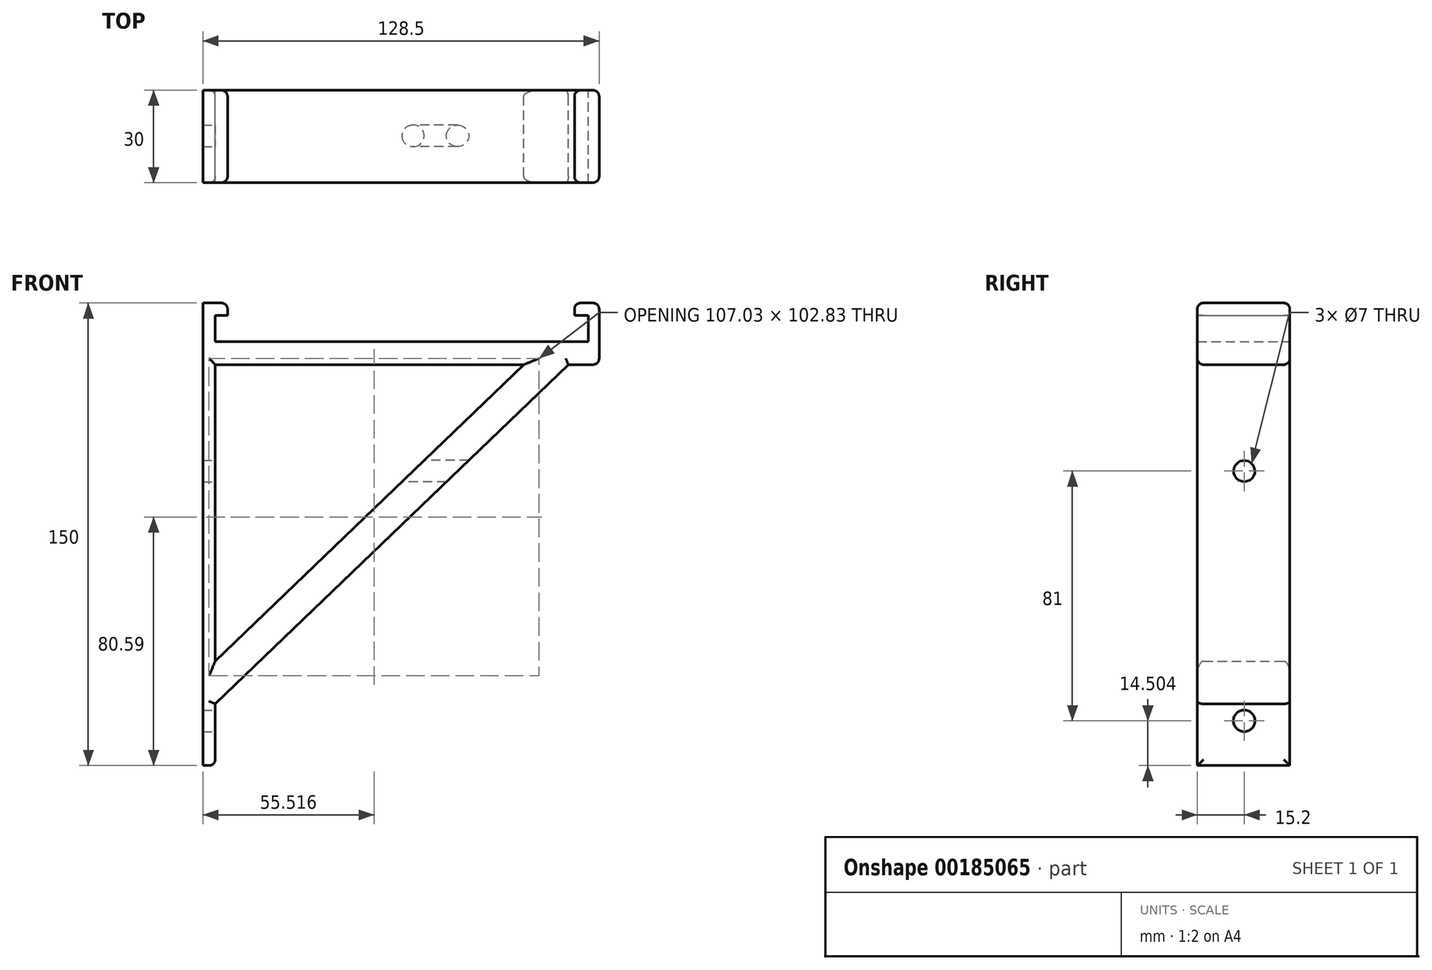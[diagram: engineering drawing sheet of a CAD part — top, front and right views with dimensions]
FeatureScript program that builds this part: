
annotation { "Feature Type Name" : "Feature", "Feature Type Description" : "" }
export const myFeature = defineFeature(function(context is Context, id is Id, definition is map)
    precondition{}
    {
        {
            var Q0;
            Q0=qCreatedBy(makeId("Front.planeOp"),FACE);
            var sketch = newSketch(context, id + "F0", { "sketchPlane" : qUnion([Q0])});
            skLineSegment(sketch, "E0", {"start": v(-57.97, 32.57) * mm, "end": v(-57.97, 24.07) * mm});
            skLineSegment(sketch, "E1", {"start": v(-57.97, 24.07) * mm, "end": v(63.03, 24.07) * mm});
            skLineSegment(sketch, "E2", {"start": v(63.03, 24.07) * mm, "end": v(63.03, 32.57) * mm});
            skLineSegment(sketch, "E3", {"start": v(63.03, 32.57) * mm, "end": v(58.53, 32.57) * mm});
            skLineSegment(sketch, "E4", {"start": v(58.53, 32.57) * mm, "end": v(58.53, 36.57) * mm});
            skLineSegment(sketch, "E5", {"start": v(58.53, 36.57) * mm, "end": v(66.53, 36.57) * mm});
            skLineSegment(sketch, "E6", {"start": v(66.53, 36.57) * mm, "end": v(66.53, 16.57) * mm});
            skLineSegment(sketch, "E7", {"start": v(-61.97, 36.57) * mm, "end": v(-53.97, 36.57) * mm});
            skLineSegment(sketch, "E8", {"start": v(-53.97, 36.57) * mm, "end": v(-53.97, 32.57) * mm});
            skLineSegment(sketch, "E9", {"start": v(-61.97, 36.57) * mm, "end": v(-61.97, 36.57) * mm});
            skLineSegment(sketch, "E10", {"start": v(-61.97, 36.57) * mm, "end": v(-61.97, -113.43) * mm});
            skLineSegment(sketch, "E11", {"start": v(-61.97, -113.43) * mm, "end": v(-61.97, -113.43) * mm});
            skLineSegment(sketch, "E12", {"start": v(66.53, 16.57) * mm, "end": v(56.53, 16.57) * mm});
            skLineSegment(sketch, "E13", {"start": v(56.53, 16.57) * mm, "end": v(-57.97, -93.43) * mm});
            skLineSegment(sketch, "E14", {"start": v(-57.97, -93.43) * mm, "end": v(-57.97, -113.43) * mm});
            skLineSegment(sketch, "E15", {"start": v(-57.97, -113.43) * mm, "end": v(-61.97, -113.43) * mm});
            skLineSegment(sketch, "E16", {"start": v(-57.97, 16.57) * mm, "end": v(-57.97, -79.56) * mm});
            skLineSegment(sketch, "E17", {"start": v(-57.97, -79.56) * mm, "end": v(42.1, 16.57) * mm});
            skLineSegment(sketch, "E18", {"start": v(42.1, 16.57) * mm, "end": v(-57.97, 16.57) * mm});
            skLineSegment(sketch, "E19", {"start": v(-53.97, 32.57) * mm, "end": v(-57.97, 32.57) * mm});
            skSolve(sketch);
        }
        {
            var Q0;
            Q0=makeQuery(id+"F0.imprint","IMPRINT",FACE,{"disambiguationData":[TD([[makeQuery(id+"F0.imprint","IMPRINT",EDGE,{"derivedFrom":sQuery(id+"F0.wireOp",EDGE,"E0")}),-1.0]])]});
            extrude(context, id + "F1", {"entities" : qUnion([Q0]), "depth" : 30 * mm});
        }
        {
            var Q0;
            Q0=qCreatedBy(makeId("Right.planeOp"),FACE);
            var sketch = newSketch(context, id + "F2", { "sketchPlane" : qUnion([Q0])});
            skCircle(sketch, "E20", {"center": v(-14.8, -98.93) * mm, "radius": 3.5 * mm});
            skCircle(sketch, "E21", {"center": v(-14.8, -17.93) * mm, "radius": 3.5 * mm});
            skSolve(sketch);
        }
        {
            var Q0;
            Q0 = qSketchRegion(id + "F2", true);
            extrude(context, id + "F3", {"entities" : qUnion([Q0]), "operationType" : NewBodyOperationType.REMOVE, "oppositeDirection" : true, "depth" : 73.1 * mm});
        }
        {
            var Q0;
            Q0 = qSketchRegion(id + "F2", true);
            extrude(context, id + "F4", {"entities" : qUnion([Q0]), "operationType" : NewBodyOperationType.REMOVE, "depth" : 25 * mm, "hasSecondDirection" : true, "secondDirectionOppositeDirection" : true, "secondDirectionDepth" : 25 * mm});
        }
        {
            var Q0;
            Q0=makeQuery(id+"F1.opExtrude","SWEPT_EDGE",EDGE,{"disambiguationData":[OSD([sQuery(id+"F0.wireOp",EDGE,"E5"),sQuery(id+"F0.wireOp",EDGE,"E6")])]});
            var Q1;
            Q1=makeQuery(id+"F1.opExtrude","SWEPT_EDGE",EDGE,{"disambiguationData":[OSD([sQuery(id+"F0.wireOp",EDGE,"E4"),sQuery(id+"F0.wireOp",EDGE,"E5")])]});
            var Q2;
            Q2=makeQuery(id+"F1.opExtrude","CAP_EDGE",EDGE,{"disambiguationData":[OSD([sQuery(id+"F0.wireOp",EDGE,"E6")])],"isStart":false});
            var Q3;
            Q3=makeQuery(id+"F1.opExtrude","CAP_EDGE",EDGE,{"disambiguationData":[OSD([sQuery(id+"F0.wireOp",EDGE,"E5")])],"isStart":false});
            var Q4;
            Q4=makeQuery(id+"F1.opExtrude","CAP_EDGE",EDGE,{"disambiguationData":[OSD([sQuery(id+"F0.wireOp",EDGE,"E5")])],"isStart":true});
            var Q5;
            Q5=makeQuery(id+"F1.opExtrude","CAP_EDGE",EDGE,{"disambiguationData":[OSD([sQuery(id+"F0.wireOp",EDGE,"E6")])],"isStart":true});
            var Q6;
            Q6=makeQuery(id+"F1.opExtrude","CAP_EDGE",EDGE,{"disambiguationData":[OSD([sQuery(id+"F0.wireOp",EDGE,"E4")])],"isStart":true});
            var Q7;
            Q7=makeQuery(id+"F1.opExtrude","CAP_EDGE",EDGE,{"disambiguationData":[OSD([sQuery(id+"F0.wireOp",EDGE,"E4")])],"isStart":false});
            var Q8;
            Q8=makeQuery(id+"F1.opExtrude","SWEPT_EDGE",EDGE,{"disambiguationData":[OSD([sQuery(id+"F0.wireOp",EDGE,"E6"),sQuery(id+"F0.wireOp",EDGE,"E12")])]});
            var Q9;
            Q9=makeQuery(id+"F1.opExtrude","CAP_EDGE",EDGE,{"disambiguationData":[OSD([sQuery(id+"F0.wireOp",EDGE,"E12")])],"isStart":false});
            var Q10;
            Q10=makeQuery(id+"F1.opExtrude","CAP_EDGE",EDGE,{"disambiguationData":[OSD([sQuery(id+"F0.wireOp",EDGE,"E12")])],"isStart":true});
            var Q11;
            Q11=makeQuery(id+"F1.opExtrude","CAP_EDGE",EDGE,{"disambiguationData":[OSD([sQuery(id+"F0.wireOp",EDGE,"E18")])],"isStart":false});
            var Q12;
            Q12=makeQuery(id+"F1.opExtrude","CAP_EDGE",EDGE,{"disambiguationData":[OSD([sQuery(id+"F0.wireOp",EDGE,"E18")])],"isStart":true});
            var Q13;
            Q13=makeQuery(id+"F1.opExtrude","CAP_EDGE",EDGE,{"disambiguationData":[OSD([sQuery(id+"F0.wireOp",EDGE,"E13")])],"isStart":false});
            var Q14;
            Q14=makeQuery(id+"F1.opExtrude","CAP_EDGE",EDGE,{"disambiguationData":[OSD([sQuery(id+"F0.wireOp",EDGE,"E17")])],"isStart":false});
            var Q15;
            Q15=makeQuery(id+"F1.opExtrude","CAP_EDGE",EDGE,{"disambiguationData":[OSD([sQuery(id+"F0.wireOp",EDGE,"E16")])],"isStart":false});
            var Q16;
            Q16=makeQuery(id+"F1.opExtrude","CAP_EDGE",EDGE,{"disambiguationData":[OSD([sQuery(id+"F0.wireOp",EDGE,"E16")])],"isStart":true});
            var Q17;
            Q17=makeQuery(id+"F1.opExtrude","CAP_EDGE",EDGE,{"disambiguationData":[OSD([sQuery(id+"F0.wireOp",EDGE,"E13")])],"isStart":true});
            var Q18;
            Q18=makeQuery(id+"F1.opExtrude","CAP_EDGE",EDGE,{"disambiguationData":[OSD([sQuery(id+"F0.wireOp",EDGE,"E17")])],"isStart":true});
            var Q19;
            Q19=makeQuery(id+"F1.opExtrude","SWEPT_EDGE",EDGE,{"disambiguationData":[OSD([sQuery(id+"F0.wireOp",EDGE,"E14"),sQuery(id+"F0.wireOp",EDGE,"E15")])]});
            var Q20;
            Q20=makeQuery(id+"F1.opExtrude","CAP_EDGE",EDGE,{"disambiguationData":[OSD([sQuery(id+"F0.wireOp",EDGE,"E14")])],"isStart":true});
            var Q21;
            Q21=makeQuery(id+"F1.opExtrude","CAP_EDGE",EDGE,{"disambiguationData":[OSD([sQuery(id+"F0.wireOp",EDGE,"E14")])],"isStart":false});
            var Q22;
            Q22=makeQuery(id+"F1.opExtrude","CAP_EDGE",EDGE,{"disambiguationData":[OSD([sQuery(id+"F0.wireOp",EDGE,"E7")])],"isStart":true});
            var Q23;
            Q23=makeQuery(id+"F1.opExtrude","CAP_EDGE",EDGE,{"disambiguationData":[OSD([sQuery(id+"F0.wireOp",EDGE,"E8")])],"isStart":true});
            var Q24;
            Q24=makeQuery(id+"F1.opExtrude","SWEPT_EDGE",EDGE,{"disambiguationData":[OSD([sQuery(id+"F0.wireOp",EDGE,"E7"),sQuery(id+"F0.wireOp",EDGE,"E8")])]});
            var Q25;
            Q25=makeQuery(id+"F1.opExtrude","CAP_EDGE",EDGE,{"disambiguationData":[OSD([sQuery(id+"F0.wireOp",EDGE,"E7")])],"isStart":false});
            var Q26;
            Q26=makeQuery(id+"F1.opExtrude","CAP_EDGE",EDGE,{"disambiguationData":[OSD([sQuery(id+"F0.wireOp",EDGE,"E8")])],"isStart":false});
            fillet(context, id + "F5", {"entities" : qUnion([Q0, Q1, Q2, Q3, Q4, Q5, Q6, Q7, Q8, Q9, Q10, Q11, Q12, Q13, Q14, Q15, Q16, Q17, Q18, Q19, Q20, Q21, Q22, Q23, Q24, Q25, Q26]), "radius" : 2 * mm, "tangentPropagation" : true, "allowEdgeOverflow" : false});
        }
    });
